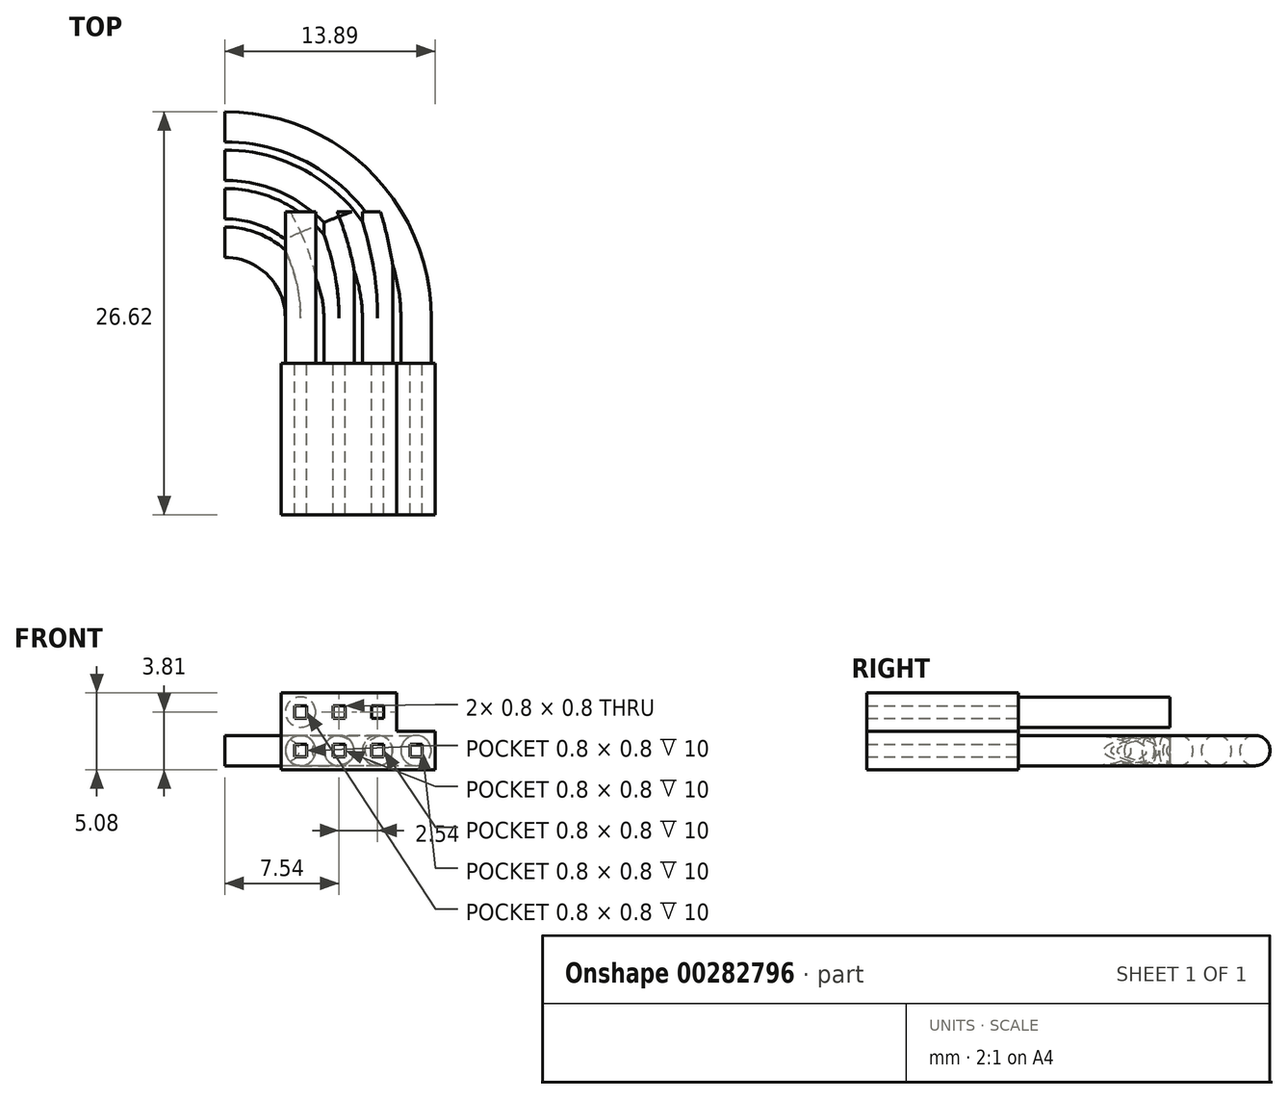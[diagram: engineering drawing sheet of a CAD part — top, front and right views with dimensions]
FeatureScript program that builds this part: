
annotation { "Feature Type Name" : "Feature", "Feature Type Description" : "" }
export const myFeature = defineFeature(function(context is Context, id is Id, definition is map)
    precondition{}
    {
        {
            var Q0;
            Q0=qCreatedBy(makeId("Front.planeOp"),FACE);
            var sketch = newSketch(context, id + "F0", { "sketchPlane" : qUnion([Q0])});
            skLineSegment(sketch, "E0.bottom", {"start": v(0.4, -0.4) * mm, "end": v(-0.4, -0.4) * mm});
            skLineSegment(sketch, "E0.top", {"start": v(0.4, 0.4) * mm, "end": v(-0.4, 0.4) * mm});
            skLineSegment(sketch, "E0.left", {"start": v(0.4, -0.4) * mm, "end": v(0.4, 0.4) * mm});
            skLineSegment(sketch, "E0.right", {"start": v(-0.4, -0.4) * mm, "end": v(-0.4, 0.4) * mm});
            skPoint(sketch, "E0.middle", {"position": v(0, 0) * mm});
            skLineSegment(sketch, "E1.bottom", {"start": v(-1.27, 1.27) * mm, "end": v(1.27, 1.27) * mm});
            skLineSegment(sketch, "E1.top", {"start": v(-1.27, -1.27) * mm, "end": v(1.27, -1.27) * mm});
            skLineSegment(sketch, "E1.left", {"start": v(-1.27, 1.27) * mm, "end": v(-1.27, -1.27) * mm});
            skLineSegment(sketch, "E1.right", {"start": v(1.27, 1.27) * mm, "end": v(1.27, -1.27) * mm});
            skLineSegment(sketch, "E2.1.0.0", {"start": v(2.94, 0.4) * mm, "end": v(2.14, 0.4) * mm});
            skLineSegment(sketch, "E2.1.0.1", {"start": v(2.94, -0.4) * mm, "end": v(2.94, 0.4) * mm});
            skLineSegment(sketch, "E2.1.0.2", {"start": v(2.14, -0.4) * mm, "end": v(2.14, 0.4) * mm});
            skLineSegment(sketch, "E2.1.0.3", {"start": v(1.27, 1.27) * mm, "end": v(3.81, 1.27) * mm});
            skLineSegment(sketch, "E2.1.0.4", {"start": v(1.27, -1.27) * mm, "end": v(3.8, -1.27) * mm});
            skLineSegment(sketch, "E2.1.0.5", {"start": v(2.94, -0.4) * mm, "end": v(2.14, -0.4) * mm});
            skPoint(sketch, "E2.1.0.6", {"position": v(2.54, 0) * mm});
            skLineSegment(sketch, "E2.1.0.8", {"start": v(3.81, 1.27) * mm, "end": v(3.8, -1.27) * mm});
            skPoint(sketch, "E2.1.0.9", {"position": v(2.54, 0) * mm});
            skLineSegment(sketch, "E2.2.0.0", {"start": v(5.48, 0.4) * mm, "end": v(4.68, 0.4) * mm});
            skLineSegment(sketch, "E2.2.0.1", {"start": v(5.48, -0.4) * mm, "end": v(5.48, 0.4) * mm});
            skLineSegment(sketch, "E2.2.0.2", {"start": v(4.68, -0.4) * mm, "end": v(4.68, 0.4) * mm});
            skLineSegment(sketch, "E2.2.0.3", {"start": v(3.8, 1.27) * mm, "end": v(6.35, 1.27) * mm});
            skLineSegment(sketch, "E2.2.0.4", {"start": v(3.8, -1.27) * mm, "end": v(6.35, -1.27) * mm});
            skLineSegment(sketch, "E2.2.0.5", {"start": v(5.48, -0.4) * mm, "end": v(4.68, -0.4) * mm});
            skPoint(sketch, "E2.2.0.6", {"position": v(5.08, 0) * mm});
            skLineSegment(sketch, "E2.2.0.7", {"start": v(3.8, 1.27) * mm, "end": v(3.8, -1.27) * mm});
            skLineSegment(sketch, "E2.2.0.8", {"start": v(6.35, 1.27) * mm, "end": v(6.35, -1.27) * mm});
            skPoint(sketch, "E2.2.0.9", {"position": v(5.08, 0) * mm});
            skLineSegment(sketch, "E2.3.0.0", {"start": v(8.02, 0.4) * mm, "end": v(7.22, 0.4) * mm});
            skLineSegment(sketch, "E2.3.0.1", {"start": v(8.02, -0.4) * mm, "end": v(8.02, 0.4) * mm});
            skLineSegment(sketch, "E2.3.0.2", {"start": v(7.22, -0.4) * mm, "end": v(7.22, 0.4) * mm});
            skLineSegment(sketch, "E2.3.0.3", {"start": v(6.35, 1.27) * mm, "end": v(8.89, 1.27) * mm});
            skLineSegment(sketch, "E2.3.0.4", {"start": v(6.35, -1.27) * mm, "end": v(8.89, -1.27) * mm});
            skLineSegment(sketch, "E2.3.0.5", {"start": v(8.02, -0.4) * mm, "end": v(7.22, -0.4) * mm});
            skPoint(sketch, "E2.3.0.6", {"position": v(7.62, 0) * mm});
            skLineSegment(sketch, "E2.3.0.7", {"start": v(6.35, 1.27) * mm, "end": v(6.35, -1.27) * mm});
            skLineSegment(sketch, "E2.3.0.8", {"start": v(8.89, 1.27) * mm, "end": v(8.89, -1.27) * mm});
            skPoint(sketch, "E2.3.0.9", {"position": v(7.62, 0) * mm});
            skLineSegment(sketch, "E2.direction1", {"start": v(-1.27, -1.27) * mm, "end": v(1.27, -1.27) * mm, "construction": true});
            skSolve(sketch);
        }
        {
            var Q0;
            Q0=qSketchRegion(id+"F0",true);
            extrude(context, id + "F1", {"entities" : qUnion([Q0]), "depth" : 10 * mm});
        }
        {
            var Q0;
            Q0=qCreatedBy(makeId("Front.planeOp"),FACE);
            var sketch = newSketch(context, id + "F2", { "sketchPlane" : qUnion([Q0])});
            skCircle(sketch, "E3", {"center": v(0, 0) * mm, "radius": 1 * mm});
            skCircle(sketch, "E4.1.0.0", {"center": v(2.54, 0) * mm, "radius": 1 * mm});
            skCircle(sketch, "E4.2.0.0", {"center": v(5.08, 0) * mm, "radius": 1 * mm});
            skCircle(sketch, "E4.3.0.0", {"center": v(7.62, 0) * mm, "radius": 1 * mm});
            skLineSegment(sketch, "E4.direction1", {"start": v(0, 0) * mm, "end": v(2.54, 0) * mm, "construction": true});
            skSolve(sketch);
        }
        {
            var Q0;
            Q0=qCreatedBy(makeId("Top.planeOp"),FACE);
            var sketch = newSketch(context, id + "F3", { "sketchPlane" : qUnion([Q0])});
            skLineSegment(sketch, "E5", {"start": v(0, 0) * mm, "end": v(0, 3) * mm});
            skLineSegment(sketch, "E6", {"start": v(-5, 8) * mm, "end": v(-20, 8) * mm, "construction": true});
            skPoint(sketch, "E7.visualSharp", {"position": v(0, 8) * mm});
            skArc(sketch, "E7.filletArc", {"start": v(0, 3) * mm, "mid": v(-1.46, 6.54) * mm, "end": v(-5, 8) * mm});
            skLineSegment(sketch, "E8.0", {"start": v(-5, 10.2) * mm, "end": v(-20, 10.2) * mm, "construction": true});
            skArc(sketch, "E8.1", {"start": v(2.2, 3) * mm, "mid": v(0.1, 8.1) * mm, "end": v(-5, 10.2) * mm});
            skLineSegment(sketch, "E8.2", {"start": v(2.2, 0) * mm, "end": v(2.2, 3) * mm});
            skLineSegment(sketch, "E9.0", {"start": v(-5, 12.4) * mm, "end": v(-20, 12.4) * mm, "construction": true});
            skArc(sketch, "E9.1", {"start": v(4.4, 3) * mm, "mid": v(1.65, 9.65) * mm, "end": v(-5, 12.4) * mm});
            skLineSegment(sketch, "E9.2", {"start": v(4.4, 0) * mm, "end": v(4.4, 3) * mm});
            skLineSegment(sketch, "E10.0", {"start": v(-5, 14.6) * mm, "end": v(-20, 14.6) * mm, "construction": true});
            skArc(sketch, "E10.1", {"start": v(6.6, 3) * mm, "mid": v(3.2, 11.2) * mm, "end": v(-5, 14.6) * mm});
            skLineSegment(sketch, "E10.2", {"start": v(6.6, 0) * mm, "end": v(6.6, 3) * mm});
            skSolve(sketch);
        }
        {
            var Q0;
            Q0=makeQuery(id+"F2.imprint","IMPRINT",FACE,{"disambiguationData":[TD([[makeQuery(id+"F2.imprint","IMPRINT",EDGE,{"derivedFrom":sQuery(id+"F2.wireOp",EDGE,"E3")}),1.0]])]});
            var Q1;
            Q1=sQuery(id+"F3.wireOp",EDGE,"E5");
            var Q2;
            Q2=sQuery(id+"F3.wireOp",EDGE,"E7.filletArc");
            var Q3;
            Q3=sQuery(id+"F3.wireOp",EDGE,"E6");
            sweep(context, id + "F4", {"operationType" : NewBodyOperationType.ADD, "profiles" : qUnion([Q0]), "path" : qUnion([Q1, Q2, Q3])});
        }
        {
            var Q0;
            Q0=makeQuery(id+"F2.imprint","IMPRINT",FACE,{"disambiguationData":[TD([[makeQuery(id+"F2.imprint","IMPRINT",EDGE,{"derivedFrom":sQuery(id+"F2.wireOp",EDGE,"E4.1.0.0")}),1.0]])]});
            var Q1;
            Q1=sQuery(id+"F3.wireOp",EDGE,"E8.2");
            var Q2;
            Q2=sQuery(id+"F3.wireOp",EDGE,"E8.1");
            var Q3;
            Q3=sQuery(id+"F3.wireOp",EDGE,"E8.0");
            sweep(context, id + "F5", {"operationType" : NewBodyOperationType.ADD, "profiles" : qUnion([Q0]), "path" : qUnion([Q1, Q2, Q3])});
        }
        {
            var Q0;
            Q0=makeQuery(id+"F2.imprint","IMPRINT",FACE,{"disambiguationData":[TD([[makeQuery(id+"F2.imprint","IMPRINT",EDGE,{"derivedFrom":sQuery(id+"F2.wireOp",EDGE,"E4.2.0.0")}),1.0]])]});
            var Q1;
            Q1=sQuery(id+"F3.wireOp",EDGE,"E9.2");
            var Q2;
            Q2=sQuery(id+"F3.wireOp",EDGE,"E9.1");
            var Q3;
            Q3=sQuery(id+"F3.wireOp",EDGE,"E9.0");
            sweep(context, id + "F6", {"operationType" : NewBodyOperationType.ADD, "profiles" : qUnion([Q0]), "path" : qUnion([Q1, Q2, Q3])});
        }
        {
            var Q0;
            Q0=makeQuery(id+"F2.imprint","IMPRINT",FACE,{"disambiguationData":[TD([[makeQuery(id+"F2.imprint","IMPRINT",EDGE,{"derivedFrom":sQuery(id+"F2.wireOp",EDGE,"E4.3.0.0")}),1.0]])]});
            var Q1;
            Q1=sQuery(id+"F3.wireOp",EDGE,"E10.2");
            var Q2;
            Q2=sQuery(id+"F3.wireOp",EDGE,"E10.1");
            var Q3;
            Q3=sQuery(id+"F3.wireOp",EDGE,"E10.0");
            sweep(context, id + "F7", {"operationType" : NewBodyOperationType.ADD, "profiles" : qUnion([Q0]), "path" : qUnion([Q1, Q2, Q3])});
        }
        {
            var Q0;
            Q0=qCreatedBy(makeId("Front.planeOp"),FACE);
            var sketch = newSketch(context, id + "F8", { "sketchPlane" : qUnion([Q0])});
            skLineSegment(sketch, "E11.bottom", {"start": v(0.4, 0.4) * mm, "end": v(-0.4, 0.4) * mm});
            skLineSegment(sketch, "E11.top", {"start": v(0.4, -0.4) * mm, "end": v(-0.4, -0.4) * mm});
            skLineSegment(sketch, "E11.left", {"start": v(0.4, 0.4) * mm, "end": v(0.4, -0.4) * mm});
            skLineSegment(sketch, "E11.right", {"start": v(-0.4, 0.4) * mm, "end": v(-0.4, -0.4) * mm});
            skPoint(sketch, "E11.middle", {"position": v(0, 0) * mm});
            skLineSegment(sketch, "E12.bottom", {"start": v(1.27, 1.27) * mm, "end": v(-1.27, 1.27) * mm});
            skLineSegment(sketch, "E12.top", {"start": v(1.27, -1.27) * mm, "end": v(-1.27, -1.27) * mm});
            skLineSegment(sketch, "E12.left", {"start": v(1.27, 1.27) * mm, "end": v(1.27, -1.27) * mm});
            skLineSegment(sketch, "E12.right", {"start": v(-1.27, 1.27) * mm, "end": v(-1.27, -1.27) * mm});
            skPoint(sketch, "E13.0.1.0", {"position": v(0, 2.54) * mm});
            skLineSegment(sketch, "E13.0.1.1", {"start": v(-1.27, 3.81) * mm, "end": v(-1.27, 1.27) * mm});
            skLineSegment(sketch, "E13.0.1.2", {"start": v(1.27, 3.81) * mm, "end": v(1.27, 1.27) * mm});
            skLineSegment(sketch, "E13.0.1.4", {"start": v(1.27, 3.81) * mm, "end": v(-1.27, 3.81) * mm});
            skPoint(sketch, "E13.0.1.5", {"position": v(0, 2.54) * mm});
            skLineSegment(sketch, "E13.0.1.6", {"start": v(-0.4, 2.94) * mm, "end": v(-0.4, 2.14) * mm});
            skLineSegment(sketch, "E13.0.1.7", {"start": v(0.4, 2.94) * mm, "end": v(0.4, 2.14) * mm});
            skLineSegment(sketch, "E13.0.1.8", {"start": v(0.4, 2.14) * mm, "end": v(-0.4, 2.14) * mm});
            skLineSegment(sketch, "E13.0.1.9", {"start": v(0.4, 2.94) * mm, "end": v(-0.4, 2.94) * mm});
            skPoint(sketch, "E13.1.0.0", {"position": v(2.54, 0) * mm});
            skLineSegment(sketch, "E13.1.0.2", {"start": v(3.81, 1.27) * mm, "end": v(3.81, -1.27) * mm});
            skLineSegment(sketch, "E13.1.0.3", {"start": v(3.81, -1.27) * mm, "end": v(1.27, -1.27) * mm});
            skLineSegment(sketch, "E13.1.0.4", {"start": v(3.81, 1.27) * mm, "end": v(1.27, 1.27) * mm});
            skPoint(sketch, "E13.1.0.5", {"position": v(2.54, 0) * mm});
            skLineSegment(sketch, "E13.1.0.6", {"start": v(2.14, 0.4) * mm, "end": v(2.14, -0.4) * mm});
            skLineSegment(sketch, "E13.1.0.7", {"start": v(2.94, 0.4) * mm, "end": v(2.94, -0.4) * mm});
            skLineSegment(sketch, "E13.1.0.8", {"start": v(2.94, -0.4) * mm, "end": v(2.14, -0.4) * mm});
            skLineSegment(sketch, "E13.1.0.9", {"start": v(2.94, 0.4) * mm, "end": v(2.14, 0.4) * mm});
            skPoint(sketch, "E13.1.1.0", {"position": v(2.54, 2.54) * mm});
            skLineSegment(sketch, "E13.1.1.1", {"start": v(1.27, 3.81) * mm, "end": v(1.27, 1.27) * mm});
            skLineSegment(sketch, "E13.1.1.2", {"start": v(3.81, 3.81) * mm, "end": v(3.81, 1.27) * mm});
            skLineSegment(sketch, "E13.1.1.3", {"start": v(3.81, 1.27) * mm, "end": v(1.27, 1.27) * mm});
            skLineSegment(sketch, "E13.1.1.4", {"start": v(3.81, 3.81) * mm, "end": v(1.27, 3.81) * mm});
            skPoint(sketch, "E13.1.1.5", {"position": v(2.54, 2.54) * mm});
            skLineSegment(sketch, "E13.1.1.6", {"start": v(2.14, 2.94) * mm, "end": v(2.14, 2.14) * mm});
            skLineSegment(sketch, "E13.1.1.7", {"start": v(2.94, 2.94) * mm, "end": v(2.94, 2.14) * mm});
            skLineSegment(sketch, "E13.1.1.8", {"start": v(2.94, 2.14) * mm, "end": v(2.14, 2.14) * mm});
            skLineSegment(sketch, "E13.1.1.9", {"start": v(2.94, 2.94) * mm, "end": v(2.14, 2.94) * mm});
            skPoint(sketch, "E13.2.0.0", {"position": v(5.08, 0) * mm});
            skLineSegment(sketch, "E13.2.0.1", {"start": v(3.8, 1.27) * mm, "end": v(3.81, -1.27) * mm});
            skLineSegment(sketch, "E13.2.0.2", {"start": v(6.35, 1.27) * mm, "end": v(6.35, -1.27) * mm});
            skLineSegment(sketch, "E13.2.0.3", {"start": v(6.35, -1.27) * mm, "end": v(3.81, -1.27) * mm});
            skLineSegment(sketch, "E13.2.0.4", {"start": v(6.35, 1.27) * mm, "end": v(3.81, 1.27) * mm});
            skPoint(sketch, "E13.2.0.5", {"position": v(5.08, 0) * mm});
            skLineSegment(sketch, "E13.2.0.6", {"start": v(4.68, 0.4) * mm, "end": v(4.68, -0.4) * mm});
            skLineSegment(sketch, "E13.2.0.7", {"start": v(5.48, 0.4) * mm, "end": v(5.48, -0.4) * mm});
            skLineSegment(sketch, "E13.2.0.8", {"start": v(5.48, -0.4) * mm, "end": v(4.68, -0.4) * mm});
            skLineSegment(sketch, "E13.2.0.9", {"start": v(5.48, 0.4) * mm, "end": v(4.68, 0.4) * mm});
            skPoint(sketch, "E13.2.1.0", {"position": v(5.08, 2.54) * mm});
            skLineSegment(sketch, "E13.2.1.1", {"start": v(3.8, 3.81) * mm, "end": v(3.81, 1.27) * mm});
            skLineSegment(sketch, "E13.2.1.2", {"start": v(6.35, 3.81) * mm, "end": v(6.35, 1.27) * mm});
            skLineSegment(sketch, "E13.2.1.3", {"start": v(6.35, 1.27) * mm, "end": v(3.81, 1.27) * mm});
            skLineSegment(sketch, "E13.2.1.4", {"start": v(6.35, 3.81) * mm, "end": v(3.81, 3.81) * mm});
            skPoint(sketch, "E13.2.1.5", {"position": v(5.08, 2.54) * mm});
            skLineSegment(sketch, "E13.2.1.6", {"start": v(4.68, 2.94) * mm, "end": v(4.68, 2.14) * mm});
            skLineSegment(sketch, "E13.2.1.7", {"start": v(5.48, 2.94) * mm, "end": v(5.48, 2.14) * mm});
            skLineSegment(sketch, "E13.2.1.8", {"start": v(5.48, 2.14) * mm, "end": v(4.68, 2.14) * mm});
            skLineSegment(sketch, "E13.2.1.9", {"start": v(5.48, 2.94) * mm, "end": v(4.68, 2.94) * mm});
            skLineSegment(sketch, "E13.direction1", {"start": v(-1.27, -1.27) * mm, "end": v(1.27, -1.27) * mm, "construction": true});
            skLineSegment(sketch, "E13.direction2", {"start": v(-1.27, -1.27) * mm, "end": v(-1.27, 1.27) * mm, "construction": true});
            skSolve(sketch);
        }
        {
            var Q0;
            Q0=qSketchRegion(id+"F8",true);
            extrude(context, id + "F9", {"entities" : qUnion([Q0]), "depth" : 10 * mm});
        }
        {
            var Q0;
            Q0=qCreatedBy(makeId("Front.planeOp"),FACE);
            var sketch = newSketch(context, id + "F10", { "sketchPlane" : qUnion([Q0])});
            skCircle(sketch, "E14", {"center": v(0, 0) * mm, "radius": 1 * mm});
            skCircle(sketch, "E15.1.0.0", {"center": v(2.54, 0) * mm, "radius": 1 * mm});
            skCircle(sketch, "E15.2.0.0", {"center": v(5.08, 0) * mm, "radius": 1 * mm});
            skLineSegment(sketch, "E15.direction1", {"start": v(0, 0) * mm, "end": v(2.54, 0) * mm, "construction": true});
            skCircle(sketch, "E16.0.1.0", {"center": v(0, 2.54) * mm, "radius": 1 * mm});
            skLineSegment(sketch, "E16.direction1", {"start": v(0, 0) * mm, "end": v(9.68, 0) * mm, "construction": true});
            skLineSegment(sketch, "E16.direction2", {"start": v(0, 0) * mm, "end": v(0, 2.54) * mm, "construction": true});
            skSolve(sketch);
        }
        {
            var Q0;
            Q0=qSketchRegion(id+"F10",true);
            extrude(context, id + "F11", {"entities" : qUnion([Q0]), "operationType" : NewBodyOperationType.ADD, "oppositeDirection" : true, "depth" : 10 * mm});
        }
    });
